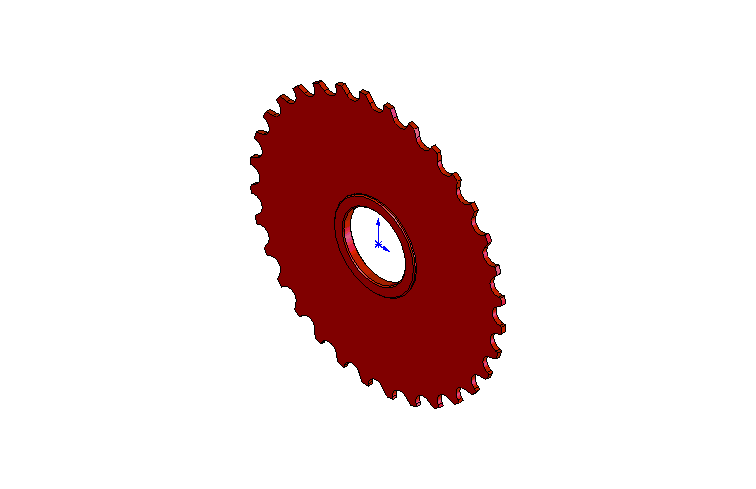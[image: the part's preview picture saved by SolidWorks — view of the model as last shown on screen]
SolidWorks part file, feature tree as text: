
SOLIDWORKS PART (.sldprt)
format: sldprt  version: not decoded by parser v0  size: 438,272 bytes
history: native  units: mm
features: sketch x4, plane x3, extrude x3, material x1, cut_extrude x1, pattern_circular x1, chamfer x1 (+10 scaffold rows collapsed)
feature tree (24):
  scaffold x10  (default folders/planes/origin — collapsed)
  material  "Matériau <non spécifié>"
  plane  "Plan de face"
  plane  "Plan de dessus"
  plane  "Plan de droite"
  sketch  "Esquisse1"  dims[D1=130.5mm]
  extrude  "Extrusion1"  Depth=2mm
  sketch  "Esquisse2"  dims[c1.D1=8.0mm c1.D3=4.0mm c2.D1=8.0mm c2.D3=4.0mm c2.D2=9.5mm c3.D3=4.0mm c3.D2=~2.039916mm c4.D2=35.0deg c4.D3=5.0mm]
  cut_extrude  "Enlèv. mat.-Extru.1"  [1 undecoded]
  pattern_circular  "Répétition circulaire1"  Count=32 Angle=11.25deg
  sketch  "Esquisse3"  dims[D1=42.0mm]
  extrude  "Extrusion2"  Depth=4.25mm
  sketch  "Esquisse4"  dims[D1=32.0mm]
  extrude  "Enlèv. mat.-Extru.2"  [1 undecoded]
  chamfer  "Chanfrein1"  Distance=0.5mm Angle=45deg
decode coverage: 8 of 10 modeling features carry decoded parameters
note: ~ marks probable driven/reference dimensions
note: 2 parameter values undecoded
note: suppression state not decoded; provenance and decode notes live in map.json
